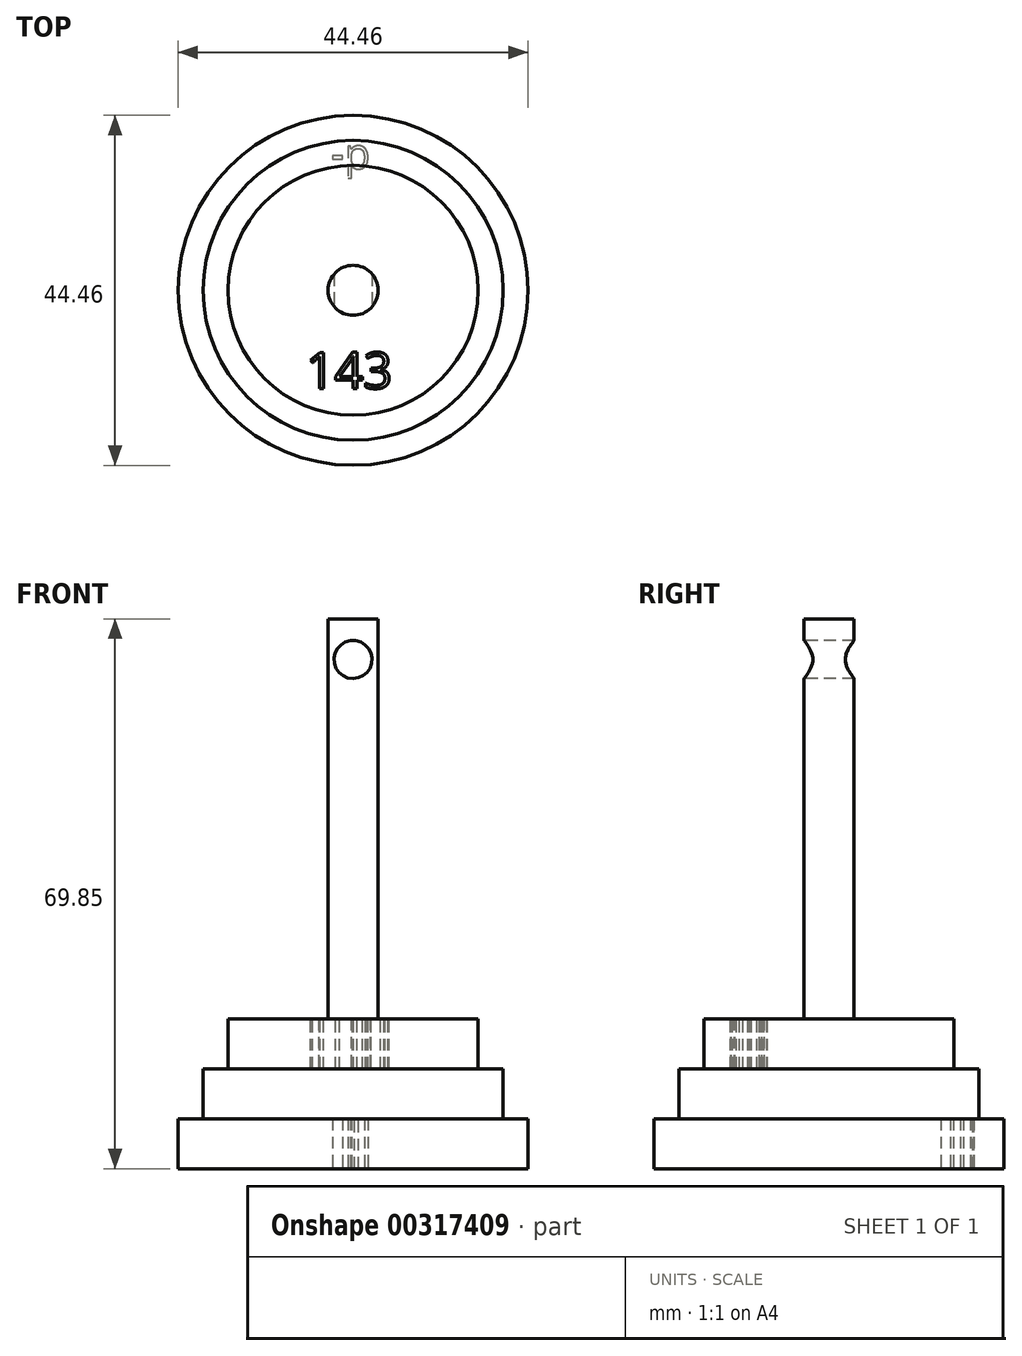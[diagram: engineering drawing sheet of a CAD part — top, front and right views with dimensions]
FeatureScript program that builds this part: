
annotation { "Feature Type Name" : "Feature", "Feature Type Description" : "" }
export const myFeature = defineFeature(function(context is Context, id is Id, definition is map)
    precondition{}
    {
        {
            var Q0;
            Q0=qCreatedBy(makeId("Top.planeOp"),FACE);
            var sketch = newSketch(context, id + "F0", { "sketchPlane" : qUnion([Q0])});
            skCircle(sketch, "E0", {"center": v(0, 0) * mm, "radius": 22.23 * mm});
            skSolve(sketch);
        }
        {
            var Q0;
            Q0=makeQuery(id+"F0.imprint","IMPRINT",FACE,{"disambiguationData":[TD([[makeQuery(id+"F0.imprint","IMPRINT",EDGE,{"derivedFrom":sQuery(id+"F0.wireOp",EDGE,"E0")}),1.0]])]});
            extrude(context, id + "F1", {"entities" : qUnion([Q0]), "depth" : 6.35 * mm});
        }
        {
            var Q0;
            Q0=makeQuery(id+"F1.opExtrude","CAP_FACE",FACE,{"disambiguationData":[OSD([sQuery(id+"F0.wireOp",EDGE,"E0")])],"isStart":false});
            var sketch = newSketch(context, id + "F2", { "sketchPlane" : qUnion([Q0])});
            skCircle(sketch, "E1", {"center": v(0, 0) * mm, "radius": 19.05 * mm});
            skSolve(sketch);
        }
        {
            var Q0;
            Q0=makeQuery(id+"F2.imprint","IMPRINT",FACE,{"disambiguationData":[TD([[makeQuery(id+"F2.imprint","IMPRINT",EDGE,{"derivedFrom":sQuery(id+"F2.wireOp",EDGE,"E1")}),1.0]])]});
            extrude(context, id + "F3", {"entities" : qUnion([Q0]), "operationType" : NewBodyOperationType.ADD, "depth" : 6.35 * mm});
        }
        {
            var Q0;
            Q0=makeQuery(id+"F3.opExtrude","CAP_FACE",FACE,{"disambiguationData":[OSD([sQuery(id+"F2.wireOp",EDGE,"E1")])],"isStart":false});
            var sketch = newSketch(context, id + "F4", { "sketchPlane" : qUnion([Q0])});
            skCircle(sketch, "E2", {"center": v(0, 0) * mm, "radius": 15.88 * mm});
            skSolve(sketch);
        }
        {
            var Q0;
            Q0 = qSketchRegion(id + "F4", true);
            extrude(context, id + "F5", {"entities" : qUnion([Q0]), "operationType" : NewBodyOperationType.ADD, "depth" : 6.35 * mm});
        }
        {
            var Q0;
            Q0=makeQuery(id+"F5.opExtrude","CAP_FACE",FACE,{"disambiguationData":[OSD([sQuery(id+"F4.wireOp",EDGE,"E2")])],"isStart":false});
            var sketch = newSketch(context, id + "F6", { "sketchPlane" : qUnion([Q0])});
            skCircle(sketch, "E3", {"center": v(0, 0) * mm, "radius": 3.18 * mm});
            skSolve(sketch);
        }
        {
            var Q0;
            Q0 = qSketchRegion(id + "F6", true);
            extrude(context, id + "F7", {"entities" : qUnion([Q0]), "operationType" : NewBodyOperationType.ADD, "depth" : 50.8 * mm});
        }
        {
            var Q0;
            Q0=qCreatedBy(makeId("Front.planeOp"),FACE);
            var sketch = newSketch(context, id + "F8", { "sketchPlane" : qUnion([Q0])});
            skCircle(sketch, "E4", {"center": v(0, 64.69) * mm, "radius": 2.42 * mm});
            skPoint(sketch, "E4.first.point", {"position": v(-2.32, 64) * mm});
            skPoint(sketch, "E4.second.point", {"position": v(2.32, 64) * mm});
            skPoint(sketch, "E4.third.point", {"position": v(0, 67.1) * mm});
            skSolve(sketch);
        }
        {
            var Q0;
            Q0 = qSketchRegion(id + "F8", true);
            extrude(context, id + "F9", {"entities" : qUnion([Q0]), "operationType" : NewBodyOperationType.REMOVE, "oppositeDirection" : true, "depth" : 25.4 * mm, "hasSecondDirection" : true, "secondDirectionOppositeDirection" : false, "secondDirectionDepth" : 25.4 * mm});
        }
        {
            var Q0;
            Q0=makeQuery(id+"F5.opExtrude","CAP_FACE",FACE,{"disambiguationData":[OSD([sQuery(id+"F4.wireOp",EDGE,"E2")])],"isStart":false});
            var sketch = newSketch(context, id + "F10", { "sketchPlane" : qUnion([Q0])});
            skText(sketch, "E5", { "text": "143", "fontName": "OpenSans-Regular.ttf"});
            const initialGuessF10  = {"E5": [-0.00601, -0.01246, 1, 0, 0.0046]};
            skSetInitialGuess(sketch, initialGuessF10);
            skSolve(sketch);
        }
        {
            var Q0;
            Q0 = qSketchRegion(id + "F10", true);
            extrude(context, id + "F11", {"entities" : qUnion([Q0]), "operationType" : NewBodyOperationType.REMOVE, "oppositeDirection" : true, "depth" : 6.35 * mm});
        }
        {
            var Q0;
            Q0=makeQuery(id+"F1.opExtrude","CAP_FACE",FACE,{"disambiguationData":[OSD([sQuery(id+"F0.wireOp",EDGE,"E0")])],"isStart":true});
            var sketch = newSketch(context, id + "F12", { "sketchPlane" : qUnion([Q0])});
            skText(sketch, "E6", { "text": "-b", "fontName": "OpenSans-Regular.ttf"});
            const initialGuessF12  = {"E6": [-0.00284, -0.01832, 1, 0, 0.00387]};
            skSetInitialGuess(sketch, initialGuessF12);
            skSolve(sketch);
        }
        {
            var Q0;
            Q0 = qSketchRegion(id + "F12", true);
            extrude(context, id + "F13", {"entities" : qUnion([Q0]), "operationType" : NewBodyOperationType.REMOVE, "oppositeDirection" : true, "depth" : 6.35 * mm});
        }
    });
